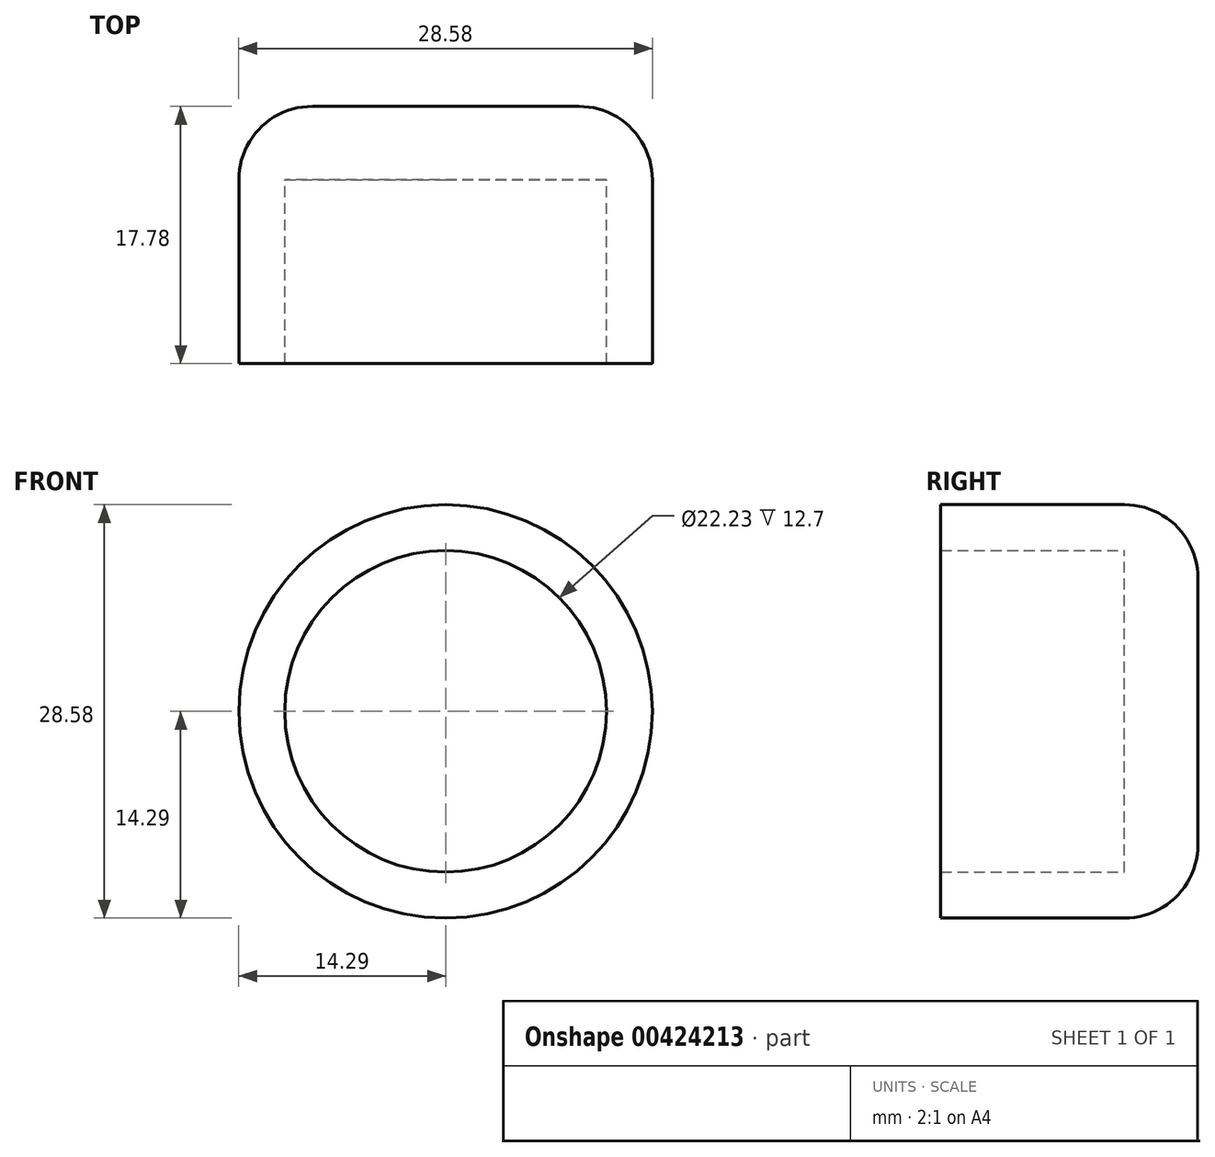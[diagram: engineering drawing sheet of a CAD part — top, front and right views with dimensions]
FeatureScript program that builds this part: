
annotation { "Feature Type Name" : "Feature", "Feature Type Description" : "" }
export const myFeature = defineFeature(function(context is Context, id is Id, definition is map)
    precondition{}
    {
        {
            var Q0;
            Q0=qCreatedBy(makeId("Front.planeOp"),FACE);
            var sketch = newSketch(context, id + "F0", { "sketchPlane" : qUnion([Q0])});
            skCircle(sketch, "E0", {"center": v(0, 0) * mm, "radius": 14.29 * mm});
            skCircle(sketch, "E1", {"center": v(0, 0) * mm, "radius": 11.11 * mm});
            skSolve(sketch);
        }
        {
            var Q0;
            Q0=makeQuery(id+"F0.imprint","IMPRINT",FACE,{"disambiguationData":[TD([[makeQuery(id+"F0.imprint","IMPRINT",EDGE,{"derivedFrom":sQuery(id+"F0.wireOp",EDGE,"E0")}),1.0]])]});
            extrude(context, id + "F1", {"entities" : qUnion([Q0]), "depth" : 12.7 * mm});
        }
        {
            var Q0;
            Q0=makeQuery(id+"F0.imprint","IMPRINT",FACE,{"disambiguationData":[TD([[makeQuery(id+"F0.imprint","IMPRINT",EDGE,{"derivedFrom":sQuery(id+"F0.wireOp",EDGE,"E1")}),1.0]])]});
            var Q1;
            Q1=makeQuery(id+"F1.opExtrude","CAP_FACE",FACE,{"disambiguationData":[OSD([sQuery(id+"F0.wireOp",EDGE,"E0"),sQuery(id+"F0.wireOp",EDGE,"E1")])],"isStart":false});
            extrude(context, id + "F2", {"entities" : qUnion([Q0, Q1]), "operationType" : NewBodyOperationType.ADD, "depth" : 5.08 * mm});
        }
        {
            var Q0;
            {var subQ0=sQuery(id+"F0.wireOp",EDGE,"E1");Q0=makeQuery(id+"F2.boolean.opBoolean","MERGE",FACE,{"derivedFrom":[makeQuery(id+"F1.opExtrude","CAP_FACE",FACE,{"disambiguationData":[OSD([sQuery(id+"F0.wireOp",EDGE,"E0"),subQ0])],"isStart":true}),makeQuery(id+"F2.opExtrude","CAP_FACE",FACE,{"disambiguationData":[OSD([subQ0])],"isStart":true})]});}
            fillet(context, id + "F3", {"entities" : qUnion([Q0]), "radius" : 5.08 * mm, "tangentPropagation" : true, "allowEdgeOverflow" : false});
        }
    });
